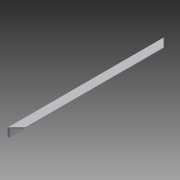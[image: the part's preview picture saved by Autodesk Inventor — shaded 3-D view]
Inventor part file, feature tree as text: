
AUTODESK INVENTOR PART (.ipt)
format: ipt  version: 2014 (Build 180170000, 170)  size: 84,480 bytes
history: native  units: in
note: dims shown in document units (in); Inventor stores cm internally (conversion verified against a paired STEP export)
features: extrude x2, sketch x2
ambient origin geometry x8: Origin, YZ Plane, XZ Plane, XY Plane, X Axis, Y Axis, Z Axis, Center Point
bodies: Solid1 (feature_tree)
feature tree (4):
  extrude  "Extrusion1"  Depth=0.5in
  extrude  "Extrusion2"  Depth=0.45in
  sketch  "Sketch1"  dims[d0=0.5in d1=0.5in]
  sketch  "Sketch2"  dims[d2=0.05in d3=0.45in d4=9.0in d5=0.0in d6=45.0deg d7=45.0deg d8=9.0in d9=0.0in]
